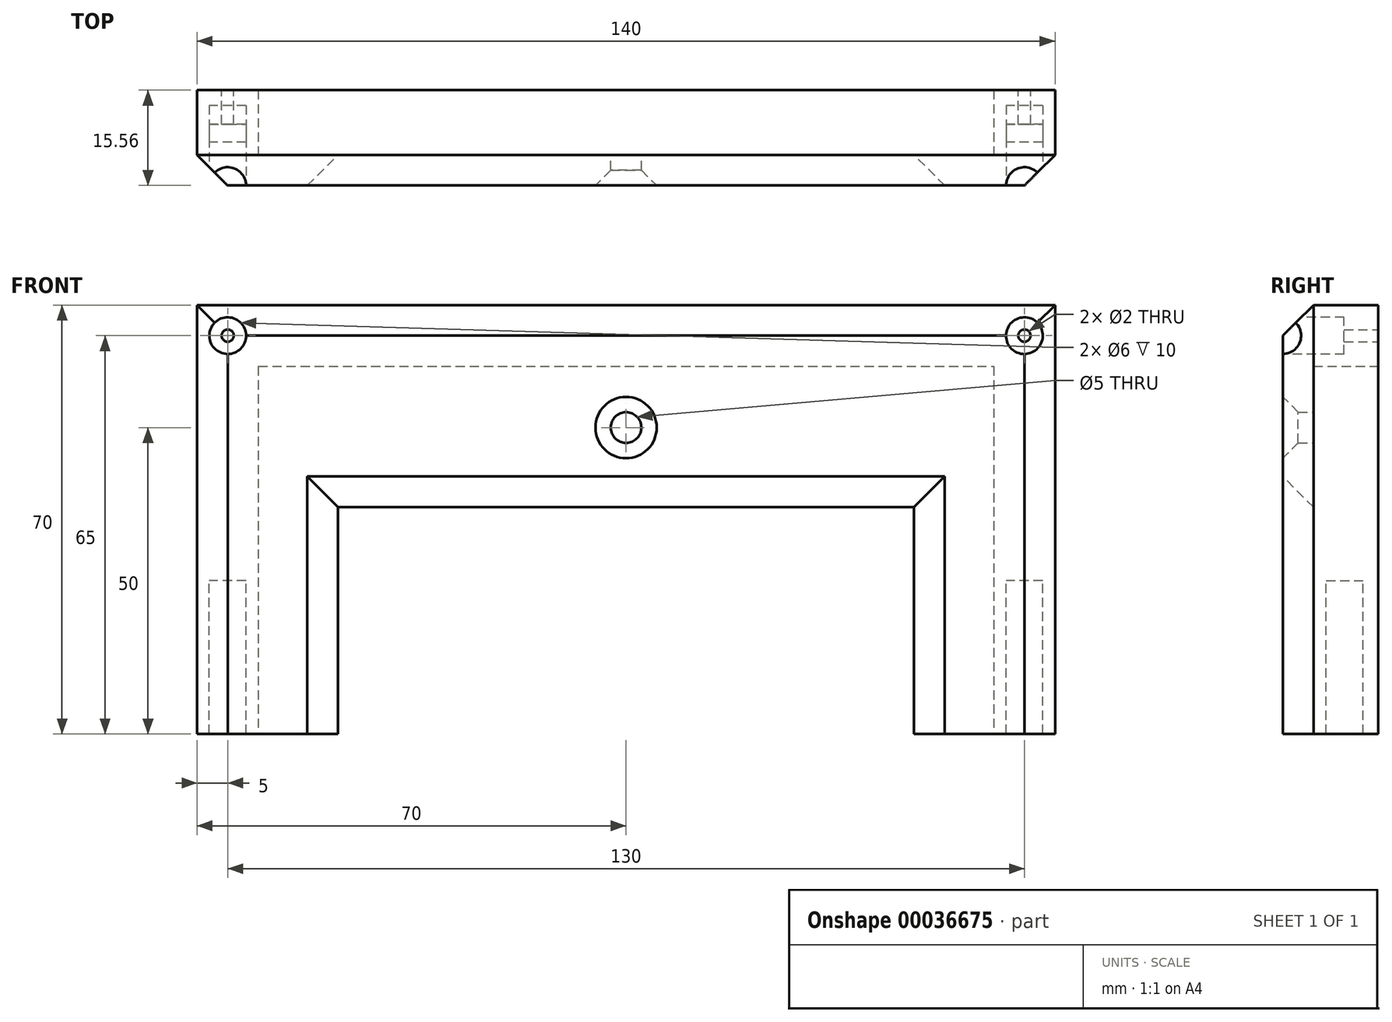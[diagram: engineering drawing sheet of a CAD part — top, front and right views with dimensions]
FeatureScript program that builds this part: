
annotation { "Feature Type Name" : "Feature", "Feature Type Description" : "" }
export const myFeature = defineFeature(function(context is Context, id is Id, definition is map)
    precondition{}
    {
        {
            var Q0;
            Q0=qCreatedBy(makeId("Front.planeOp"),FACE);
            var sketch = newSketch(context, id + "F0", { "sketchPlane" : qUnion([Q0])});
            skLineSegment(sketch, "E0.bottom", {"start": v(0, 0) * mm, "end": v(-140, 0) * mm});
            skLineSegment(sketch, "E0.top", {"start": v(0, 252.5) * mm, "end": v(-140, 252.5) * mm});
            skLineSegment(sketch, "E0.left", {"start": v(0, 0) * mm, "end": v(0, 252.5) * mm});
            skLineSegment(sketch, "E0.right", {"start": v(-140, 0) * mm, "end": v(-140, 252.5) * mm});
            skLineSegment(sketch, "E1.bottom", {"start": v(-130, 242.5) * mm, "end": v(-10, 242.5) * mm});
            skLineSegment(sketch, "E1.top", {"start": v(-130, 44) * mm, "end": v(-10, 44) * mm});
            skLineSegment(sketch, "E1.left", {"start": v(-130, 242.5) * mm, "end": v(-130, 44) * mm});
            skLineSegment(sketch, "E1.right", {"start": v(-10, 242.5) * mm, "end": v(-10, 44) * mm});
            skLineSegment(sketch, "E2.bottom", {"start": v(-117, 219.5) * mm, "end": v(-23, 219.5) * mm});
            skLineSegment(sketch, "E2.top", {"start": v(-117, 67) * mm, "end": v(-23, 67) * mm});
            skLineSegment(sketch, "E2.left", {"start": v(-117, 219.5) * mm, "end": v(-117, 67) * mm});
            skLineSegment(sketch, "E2.right", {"start": v(-23, 219.5) * mm, "end": v(-23, 67) * mm});
            skLineSegment(sketch, "E3.bottom", {"start": v(-76, 44) * mm, "end": v(-64, 44) * mm});
            skLineSegment(sketch, "E3.top", {"start": v(-76, 10) * mm, "end": v(-64, 10) * mm});
            skLineSegment(sketch, "E3.left", {"start": v(-76, 44) * mm, "end": v(-76, 10) * mm});
            skLineSegment(sketch, "E3.right", {"start": v(-64, 44) * mm, "end": v(-64, 10) * mm});
            skCircle(sketch, "E4", {"center": v(-70, 232.5) * mm, "radius": 2.5 * mm});
            skCircle(sketch, "E5", {"center": v(-135, 247.5) * mm, "radius": 1 * mm});
            skLineSegment(sketch, "E6.direction1", {"start": v(-135, 247.5) * mm, "end": v(-5, 247.5) * mm, "construction": true});
            skLineSegment(sketch, "E6.direction2", {"start": v(-135, 247.5) * mm, "end": v(-135, 5) * mm, "construction": true});
            skCircle(sketch, "E7.0.1.0", {"center": v(-135, 5) * mm, "radius": 1 * mm});
            skCircle(sketch, "E7.1.0.0", {"center": v(-5, 247.5) * mm, "radius": 1 * mm});
            skCircle(sketch, "E7.1.1.0", {"center": v(-5, 5) * mm, "radius": 1 * mm});
            skSolve(sketch);
        }
        {
            var Q0;
            Q0=makeQuery(id+"F0.imprint","IMPRINT",FACE,{"disambiguationData":[TD([[makeQuery(id+"F0.imprint","IMPRINT",EDGE,{"derivedFrom":sQuery(id+"F0.wireOp",EDGE,"E0.bottom")}),-1.0]])]});
            var Q1;
            Q1=makeQuery(id+"F0.imprint","IMPRINT",FACE,{"disambiguationData":[TD([[makeQuery(id+"F0.imprint","IMPRINT",EDGE,{"derivedFrom":sQuery(id+"F0.wireOp",EDGE,"E3.top")}),1.0]])]});
            var Q2;
            Q2=makeQuery(id+"F0.imprint","IMPRINT",FACE,{"disambiguationData":[TD([[makeQuery(id+"F0.imprint","IMPRINT",EDGE,{"derivedFrom":sQuery(id+"F0.wireOp",EDGE,"E1.bottom")}),-1.0]])]});
            var Q3;
            Q3=makeQuery(id+"F0.imprint","IMPRINT",FACE,{"disambiguationData":[TD([[makeQuery(id+"F0.imprint","IMPRINT",EDGE,{"derivedFrom":sQuery(id+"F0.wireOp",EDGE,"E6.1.1.0")}),1.0]])]});
            var Q4;
            Q4=makeQuery(id+"F0.imprint","IMPRINT",FACE,{"disambiguationData":[TD([[makeQuery(id+"F0.imprint","IMPRINT",EDGE,{"derivedFrom":sQuery(id+"F0.wireOp",EDGE,"E6.0.1.0")}),1.0]])]});
            var Q5;
            Q5=makeQuery(id+"F0.imprint","IMPRINT",FACE,{"disambiguationData":[TD([[makeQuery(id+"F0.imprint","IMPRINT",EDGE,{"derivedFrom":sQuery(id+"F0.wireOp",EDGE,"E6.1.0.0")}),1.0]])]});
            var Q6;
            Q6=makeQuery(id+"F0.imprint","IMPRINT",FACE,{"disambiguationData":[TD([[makeQuery(id+"F0.imprint","IMPRINT",EDGE,{"derivedFrom":sQuery(id+"F0.wireOp",EDGE,"E0.bottom")}),-1.0]])]});
            extrude(context, id + "F1", {"entities" : qUnion([Q0, Q1, Q2, Q3, Q4, Q5, Q6]), "depth" : (10.56 + 5) * mm});
        }
        {
            var Q0;
            Q0=makeQuery(id+"F0.imprint","IMPRINT",FACE,{"disambiguationData":[TD([[makeQuery(id+"F0.imprint","IMPRINT",EDGE,{"derivedFrom":sQuery(id+"F0.wireOp",EDGE,"E1.bottom")}),-1.0]])]});
            var Q1;
            Q1=makeQuery(id+"F0.imprint","IMPRINT",FACE,{"disambiguationData":[TD([[makeQuery(id+"F0.imprint","IMPRINT",EDGE,{"derivedFrom":sQuery(id+"F0.wireOp",EDGE,"E3.top")}),1.0]])]});
            extrude(context, id + "F2", {"entities" : qUnion([Q0, Q1]), "operationType" : NewBodyOperationType.REMOVE, "depth" : 10.56 * mm});
        }
        {
            var Q0;
            Q0=makeQuery(id+"F1.opExtrude","CAP_EDGE",EDGE,{"disambiguationData":[OSD([sQuery(id+"F0.wireOp",EDGE,"E0.bottom")])],"isStart":false});
            var Q1;
            Q1=makeQuery(id+"F1.opExtrude","CAP_EDGE",EDGE,{"disambiguationData":[OSD([sQuery(id+"F0.wireOp",EDGE,"E0.right")])],"isStart":false});
            var Q2;
            Q2=makeQuery(id+"F1.opExtrude","CAP_EDGE",EDGE,{"disambiguationData":[OSD([sQuery(id+"F0.wireOp",EDGE,"E0.left")])],"isStart":false});
            var Q3;
            Q3=makeQuery(id+"F1.opExtrude","CAP_EDGE",EDGE,{"disambiguationData":[OSD([sQuery(id+"F0.wireOp",EDGE,"E0.top")])],"isStart":false});
            chamfer(context, id + "F3", {"entities" : qUnion([Q0, Q1, Q2, Q3]), "width" : 5 * mm, "tangentPropagation" : true});
        }
        {
            var Q0;
            Q0=makeQuery(id+"F1.opExtrude","CAP_EDGE",EDGE,{"disambiguationData":[OSD([sQuery(id+"F0.wireOp",EDGE,"E4")])],"isStart":false});
            chamfer(context, id + "F4", {"entities" : qUnion([Q0]), "width" : 2.5 * mm, "tangentPropagation" : true});
        }
        {
            var Q0;
            Q0=makeQuery(id+"F1.opExtrude","CAP_FACE",FACE,{"disambiguationData":[OSD([sQuery(id+"F0.wireOp",EDGE,"E0.bottom"),sQuery(id+"F0.wireOp",EDGE,"E0.top"),sQuery(id+"F0.wireOp",EDGE,"E0.left"),sQuery(id+"F0.wireOp",EDGE,"E0.right"),sQuery(id+"F0.wireOp",EDGE,"E2.bottom"),sQuery(id+"F0.wireOp",EDGE,"E2.top"),sQuery(id+"F0.wireOp",EDGE,"E2.left"),sQuery(id+"F0.wireOp",EDGE,"E2.right"),sQuery(id+"F0.wireOp",EDGE,"E4"),sQuery(id+"F0.wireOp",EDGE,"E5"),sQuery(id+"F0.wireOp",EDGE,"E7.0.1.0"),sQuery(id+"F0.wireOp",EDGE,"E7.1.0.0"),sQuery(id+"F0.wireOp",EDGE,"E7.1.1.0")])],"isStart":false});
            var sketch = newSketch(context, id + "F5", { "sketchPlane" : qUnion([Q0])});
            skCircle(sketch, "E8", {"center": v(-135, 247.5) * mm, "radius": 3 * mm});
            skCircle(sketch, "E9.0.1.0", {"center": v(-135, 5) * mm, "radius": 3 * mm});
            skCircle(sketch, "E9.1.0.0", {"center": v(-5, 247.5) * mm, "radius": 3 * mm});
            skCircle(sketch, "E9.1.1.0", {"center": v(-5, 5) * mm, "radius": 3 * mm});
            skLineSegment(sketch, "E9.direction1", {"start": v(-135, 247.5) * mm, "end": v(-5, 247.5) * mm, "construction": true});
            skLineSegment(sketch, "E9.direction2", {"start": v(-135, 247.5) * mm, "end": v(-135, 5) * mm, "construction": true});
            skSolve(sketch);
        }
        {
            var Q0;
            Q0=qSketchRegion(id+"F5",true);
            extrude(context, id + "F6", {"entities" : qUnion([Q0]), "operationType" : NewBodyOperationType.REMOVE, "oppositeDirection" : true, "depth" : 10 * mm});
        }
        {
            var Q0;
            Q0=makeQuery(id+"F1.opExtrude","CAP_EDGE",EDGE,{"disambiguationData":[OSD([sQuery(id+"F0.wireOp",EDGE,"E2.top")])],"isStart":false});
            var Q1;
            Q1=makeQuery(id+"F1.opExtrude","CAP_EDGE",EDGE,{"disambiguationData":[OSD([sQuery(id+"F0.wireOp",EDGE,"E2.left")])],"isStart":false});
            var Q2;
            Q2=makeQuery(id+"F1.opExtrude","CAP_EDGE",EDGE,{"disambiguationData":[OSD([sQuery(id+"F0.wireOp",EDGE,"E2.right")])],"isStart":false});
            var Q3;
            Q3=makeQuery(id+"F1.opExtrude","CAP_EDGE",EDGE,{"disambiguationData":[OSD([sQuery(id+"F0.wireOp",EDGE,"E2.bottom")])],"isStart":false});
            chamfer(context, id + "F7", {"entities" : qUnion([Q0, Q1, Q2, Q3]), "width" : 5 * mm, "tangentPropagation" : true});
        }
        {
            var Q0;
            Q0=makeQuery(id+"F1.opExtrude","CAP_FACE",FACE,{"disambiguationData":[OSD([sQuery(id+"F0.wireOp",EDGE,"E0.bottom"),sQuery(id+"F0.wireOp",EDGE,"E0.top"),sQuery(id+"F0.wireOp",EDGE,"E0.left"),sQuery(id+"F0.wireOp",EDGE,"E0.right"),sQuery(id+"F0.wireOp",EDGE,"E2.bottom"),sQuery(id+"F0.wireOp",EDGE,"E2.top"),sQuery(id+"F0.wireOp",EDGE,"E2.left"),sQuery(id+"F0.wireOp",EDGE,"E2.right"),sQuery(id+"F0.wireOp",EDGE,"E4"),sQuery(id+"F0.wireOp",EDGE,"E5"),sQuery(id+"F0.wireOp",EDGE,"E7.0.1.0"),sQuery(id+"F0.wireOp",EDGE,"E7.1.0.0"),sQuery(id+"F0.wireOp",EDGE,"E7.1.1.0")])],"isStart":false});
            var sketch = newSketch(context, id + "F8", { "sketchPlane" : qUnion([Q0])});
            skLineSegment(sketch, "E10.bottom", {"start": v(5.81, 182.5) * mm, "end": v(-155.44, 182.5) * mm});
            skLineSegment(sketch, "E10.top", {"start": v(5.81, 0) * mm, "end": v(-155.44, 0) * mm});
            skLineSegment(sketch, "E10.left", {"start": v(5.81, 182.5) * mm, "end": v(5.81, 0) * mm});
            skLineSegment(sketch, "E10.right", {"start": v(-155.44, 182.5) * mm, "end": v(-155.44, 0) * mm});
            skSolve(sketch);
        }
        {
            var Q0;
            Q0=qSketchRegion(id+"F8",true);
            extrude(context, id + "F9", {"entities" : qUnion([Q0]), "operationType" : NewBodyOperationType.REMOVE, "oppositeDirection" : true, "depth" : 25 * mm});
        }
        {
            var Q0;
            Q0=makeQuery(id+"F1.opExtrude","CAP_FACE",FACE,{"disambiguationData":[OSD([sQuery(id+"F0.wireOp",EDGE,"E0.bottom"),sQuery(id+"F0.wireOp",EDGE,"E0.top"),sQuery(id+"F0.wireOp",EDGE,"E0.left"),sQuery(id+"F0.wireOp",EDGE,"E0.right"),sQuery(id+"F0.wireOp",EDGE,"E2.bottom"),sQuery(id+"F0.wireOp",EDGE,"E2.top"),sQuery(id+"F0.wireOp",EDGE,"E2.left"),sQuery(id+"F0.wireOp",EDGE,"E2.right"),sQuery(id+"F0.wireOp",EDGE,"E4"),sQuery(id+"F0.wireOp",EDGE,"E5"),sQuery(id+"F0.wireOp",EDGE,"E7.0.1.0"),sQuery(id+"F0.wireOp",EDGE,"E7.1.0.0"),sQuery(id+"F0.wireOp",EDGE,"E7.1.1.0")])],"isStart":true});
            cPlane(context, id + "F10", {"entities" : qUnion([Q0]), "cplaneType" : CPlaneType.OFFSET, "offset" : 2.5 * mm, "oppositeDirection" : true, "width" : 150 * mm, "height" : 150 * mm});
        }
        {
            var Q0;
            Q0=qCreatedBy(id+"F10.planeOp",FACE);
            var sketch = newSketch(context, id + "F11", { "sketchPlane" : qUnion([Q0])});
            skLineSegment(sketch, "E11.bottom", {"start": v(132, 157.5) * mm, "end": v(138, 157.5) * mm});
            skLineSegment(sketch, "E11.top", {"start": v(132, 207.5) * mm, "end": v(138, 207.5) * mm});
            skLineSegment(sketch, "E11.left", {"start": v(132, 157.5) * mm, "end": v(132, 207.5) * mm});
            skLineSegment(sketch, "E11.right", {"start": v(138, 157.5) * mm, "end": v(138, 207.5) * mm});
            skLineSegment(sketch, "E12.1.0.0", {"start": v(8, 157.5) * mm, "end": v(8, 207.5) * mm});
            skLineSegment(sketch, "E12.1.0.1", {"start": v(2, 157.5) * mm, "end": v(8, 157.5) * mm});
            skLineSegment(sketch, "E12.1.0.2", {"start": v(2, 157.5) * mm, "end": v(2, 207.5) * mm});
            skLineSegment(sketch, "E12.1.0.3", {"start": v(2, 207.5) * mm, "end": v(8, 207.5) * mm});
            skLineSegment(sketch, "E12.direction1", {"start": v(138, 157.5) * mm, "end": v(8, 157.5) * mm, "construction": true});
            skSolve(sketch);
        }
        {
            var Q0;
            Q0=qSketchRegion(id+"F11",true);
            extrude(context, id + "F12", {"entities" : qUnion([Q0]), "operationType" : NewBodyOperationType.REMOVE, "oppositeDirection" : true, "offsetDistance" : 25 * mm, "depth" : 6 * mm});
        }
    });
